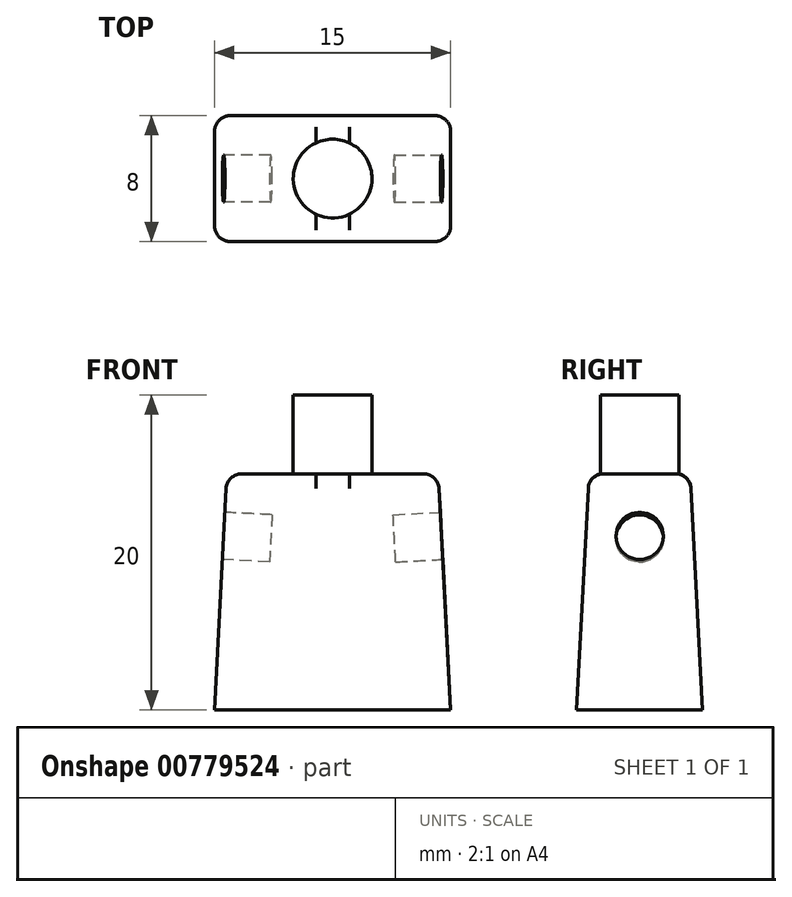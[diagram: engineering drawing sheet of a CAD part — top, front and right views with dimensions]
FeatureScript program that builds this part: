
annotation { "Feature Type Name" : "Feature", "Feature Type Description" : "" }
export const myFeature = defineFeature(function(context is Context, id is Id, definition is map)
    precondition{}
    {
        {
            var Q0;
            Q0=qCreatedBy(makeId("Top.planeOp"),FACE);
            var sketch = newSketch(context, id + "F0", { "sketchPlane" : qUnion([Q0])});
            skLineSegment(sketch, "E0.bottom", {"start": v(7.5, -4) * mm, "end": v(-7.5, -4) * mm});
            skLineSegment(sketch, "E0.top", {"start": v(7.5, 4) * mm, "end": v(-7.5, 4) * mm});
            skLineSegment(sketch, "E0.left", {"start": v(7.5, -4) * mm, "end": v(7.5, 4) * mm});
            skLineSegment(sketch, "E0.right", {"start": v(-7.5, -4) * mm, "end": v(-7.5, 4) * mm});
            skPoint(sketch, "E0.middle", {"position": v(0, 0) * mm});
            skSolve(sketch);
        }
        {
            var Q0;
            Q0 = qSketchRegion(id + "F0", true);
            extrude(context, id + "F1", {"entities" : qUnion([Q0]), "depth" : 15 * mm, "offsetDistance" : 25 * mm, "hasDraft" : true, "draftAngle" : 3 * degree, "draftPullDirection" : true});
        }
        {
            var Q0;
            Q0=makeQuery(id+"F1.opExtrude","CAP_FACE",FACE,{"disambiguationData":[OSD([sQuery(id+"F0.wireOp",EDGE,"E0.bottom"),sQuery(id+"F0.wireOp",EDGE,"E0.top"),sQuery(id+"F0.wireOp",EDGE,"E0.left"),sQuery(id+"F0.wireOp",EDGE,"E0.right")])],"isStart":false});
            var sketch = newSketch(context, id + "F2", { "sketchPlane" : qUnion([Q0])});
            skCircle(sketch, "E1", {"center": v(0, 0) * mm, "radius": 2.5 * mm});
            skSolve(sketch);
        }
        {
            var Q0;
            Q0 = qSketchRegion(id + "F2", true);
            extrude(context, id + "F3", {"entities" : qUnion([Q0]), "operationType" : NewBodyOperationType.ADD, "depth" : 5 * mm, "offsetDistance" : 25 * mm});
        }
        {
            var Q0;
            Q0=makeQuery(id+"F1.opExtrude","SWEPT_EDGE",EDGE,{"disambiguationData":[OSD([sQuery(id+"F0.wireOp",EDGE,"E0.bottom"),sQuery(id+"F0.wireOp",EDGE,"E0.right")])]});
            var Q1;
            Q1=makeQuery(id+"F1.opExtrude","SWEPT_EDGE",EDGE,{"disambiguationData":[OSD([sQuery(id+"F0.wireOp",EDGE,"E0.bottom"),sQuery(id+"F0.wireOp",EDGE,"E0.left")])]});
            var Q2;
            Q2=makeQuery(id+"F1.opExtrude","SWEPT_EDGE",EDGE,{"disambiguationData":[OSD([sQuery(id+"F0.wireOp",EDGE,"E0.top"),sQuery(id+"F0.wireOp",EDGE,"E0.right")])]});
            var Q3;
            Q3=makeQuery(id+"F1.opExtrude","SWEPT_EDGE",EDGE,{"disambiguationData":[OSD([sQuery(id+"F0.wireOp",EDGE,"E0.top"),sQuery(id+"F0.wireOp",EDGE,"E0.left")])]});
            var Q4;
            Q4=makeQuery(id+"F1.opExtrude","CAP_EDGE",EDGE,{"disambiguationData":[OSD([sQuery(id+"F0.wireOp",EDGE,"E0.left")])],"isStart":false});
            var Q5;
            Q5=makeQuery(id+"F1.opExtrude","CAP_EDGE",EDGE,{"disambiguationData":[OSD([sQuery(id+"F0.wireOp",EDGE,"E0.top")])],"isStart":false});
            var Q6;
            Q6=makeQuery(id+"F1.opExtrude","CAP_EDGE",EDGE,{"disambiguationData":[OSD([sQuery(id+"F0.wireOp",EDGE,"E0.right")])],"isStart":false});
            var Q7;
            Q7=makeQuery(id+"F1.opExtrude","CAP_EDGE",EDGE,{"disambiguationData":[OSD([sQuery(id+"F0.wireOp",EDGE,"E0.bottom")])],"isStart":false});
            fillet(context, id + "F4", {"entities" : qUnion([Q0, Q1, Q2, Q3, Q4, Q5, Q6, Q7]), "radius" : 1 * mm, "tangentPropagation" : true, "allowEdgeOverflow" : false});
        }
        {
            var Q0;
            Q0=makeQuery(id+"F1.opExtrude","SWEPT_FACE",FACE,{"disambiguationData":[OSD([sQuery(id+"F0.wireOp",EDGE,"E0.left")])]});
            var sketch = newSketch(context, id + "F5", { "sketchPlane" : qUnion([Q0])});
            skCircle(sketch, "E2", {"center": v(0, 10.68) * mm, "radius": 1.5 * mm});
            skSolve(sketch);
        }
        {
            var Q0;
            Q0 = qSketchRegion(id + "F5", true);
            extrude(context, id + "F6", {"entities" : qUnion([Q0]), "operationType" : NewBodyOperationType.REMOVE, "oppositeDirection" : true, "depth" : 3 * mm, "offsetDistance" : 25 * mm});
        }
        {
            var Q0;
            Q0=makeQuery(id+"F1.opExtrude","SWEPT_FACE",FACE,{"disambiguationData":[OSD([sQuery(id+"F0.wireOp",EDGE,"E0.right")])]});
            var sketch = newSketch(context, id + "F7", { "sketchPlane" : qUnion([Q0])});
            skCircle(sketch, "E3", {"center": v(0, 10.68) * mm, "radius": 1.5 * mm});
            skSolve(sketch);
        }
        {
            var Q0;
            Q0 = qSketchRegion(id + "F7", true);
            extrude(context, id + "F8", {"entities" : qUnion([Q0]), "operationType" : NewBodyOperationType.REMOVE, "oppositeDirection" : true, "depth" : 3 * mm, "offsetDistance" : 25 * mm});
        }
    });
